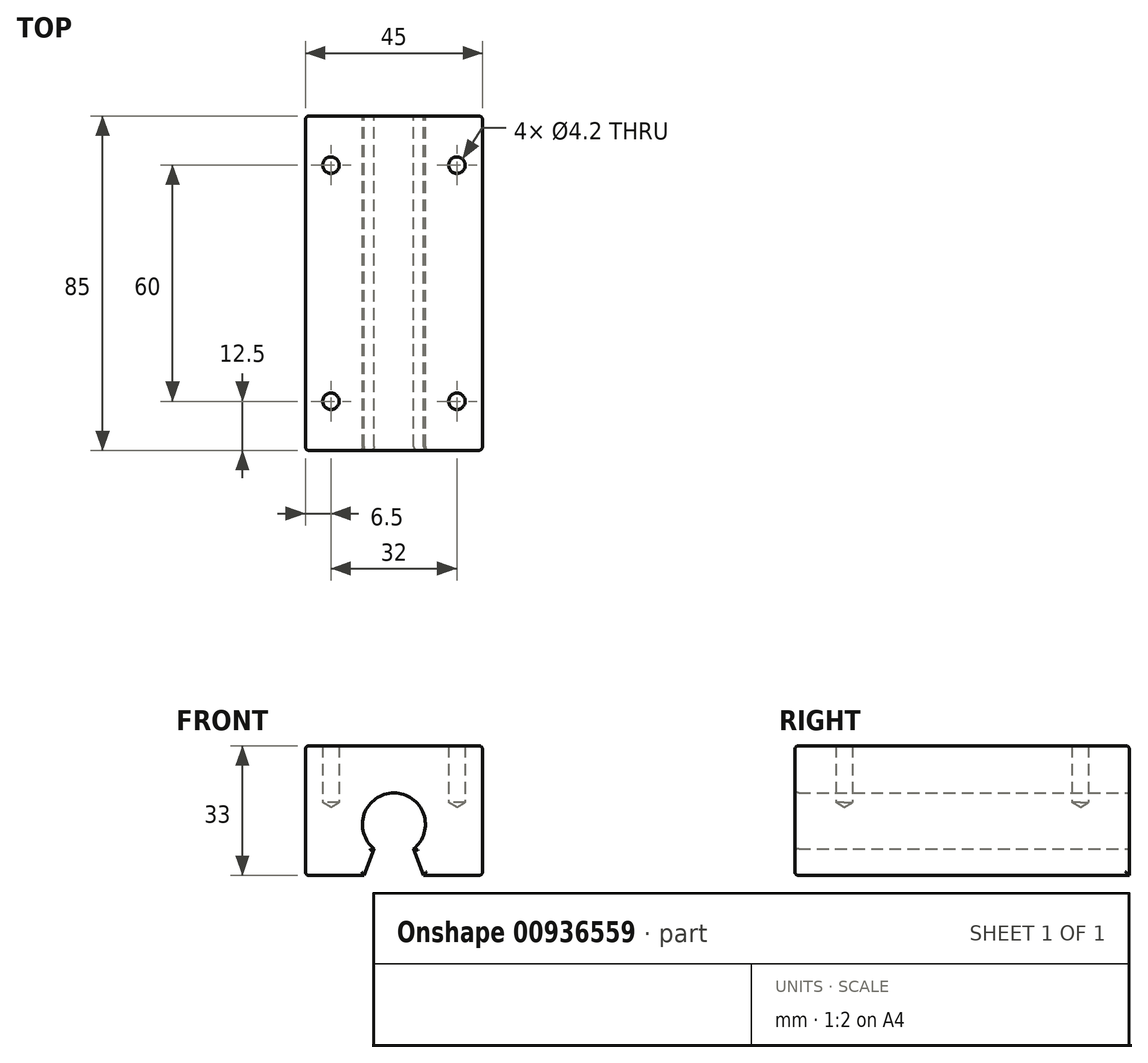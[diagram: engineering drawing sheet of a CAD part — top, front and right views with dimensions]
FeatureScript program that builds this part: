
annotation { "Feature Type Name" : "Feature", "Feature Type Description" : "" }
export const myFeature = defineFeature(function(context is Context, id is Id, definition is map)
    precondition{}
    {
        {
            var Q0;
            Q0=qCreatedBy(makeId("Front.planeOp"),FACE);
            var sketch = newSketch(context, id + "F0", { "sketchPlane" : qUnion([Q0])});
            skLineSegment(sketch, "E0.bottom", {"start": v(-22.5, 16.5) * mm, "end": v(22.5, 16.5) * mm});
            skLineSegment(sketch, "E0.top", {"start": v(-22.5, -16.5) * mm, "end": v(-7.57, -16.5) * mm});
            skLineSegment(sketch, "E0.left", {"start": v(-22.5, 16.5) * mm, "end": v(-22.5, -16.5) * mm});
            skLineSegment(sketch, "E0.right", {"start": v(22.5, 16.5) * mm, "end": v(22.5, -16.5) * mm});
            skPoint(sketch, "E0.middle", {"position": v(0, 0) * mm});
            skArc(sketch, "E1", {"start": v(5, -9.74) * mm, "mid": v(0, 4.5) * mm, "end": v(-5, -9.74) * mm});
            skLineSegment(sketch, "E2", {"start": v(-5, -9.74) * mm, "end": v(-7.57, -16.5) * mm});
            skPoint(sketch, "E3.MirrorP", {"position": v(-2.27, 0.86) * mm});
            skLineSegment(sketch, "E4", {"start": v(0, 23.1) * mm, "end": v(0, -23.77) * mm, "construction": true});
            skLineSegment(sketch, "E5.MirrorCS", {"start": v(5, -9.74) * mm, "end": v(7.57, -16.5) * mm});
            skLineSegment(sketch, "E6.trimOffspring", {"start": v(7.57, -16.5) * mm, "end": v(22.5, -16.5) * mm});
            skSolve(sketch);
        }
        {
            var Q0;
            Q0=makeQuery(id+"F0.imprint","IMPRINT",FACE,{"disambiguationData":[TD([[makeQuery(id+"F0.imprint","IMPRINT",EDGE,{"derivedFrom":sQuery(id+"F0.wireOp",EDGE,"E0.bottom")}),-1.0]])]});
            extrude(context, id + "F1", {"entities" : qUnion([Q0]), "depth" : 85 * mm, "offsetDistance" : 25 * mm});
        }
        {
            var Q0;
            Q0=makeQuery(id+"F1.opExtrude","SWEPT_FACE",FACE,{"disambiguationData":[OSD([sQuery(id+"F0.wireOp",EDGE,"E0.left")])]});
            var Q1;
            Q1=makeQuery(id+"F1.opExtrude","SWEPT_FACE",FACE,{"disambiguationData":[OSD([sQuery(id+"F0.wireOp",EDGE,"E0.bottom")])]});
            var Q2;
            Q2=makeQuery(id+"F1.opExtrude","CAP_FACE",FACE,{"disambiguationData":[OSD([sQuery(id+"F0.wireOp",EDGE,"E0.bottom"),sQuery(id+"F0.wireOp",EDGE,"E0.top"),sQuery(id+"F0.wireOp",EDGE,"E0.left"),sQuery(id+"F0.wireOp",EDGE,"E0.right"),sQuery(id+"F0.wireOp",EDGE,"E1"),sQuery(id+"F0.wireOp",EDGE,"E2"),sQuery(id+"F0.wireOp",EDGE,"E5.MirrorCS"),sQuery(id+"F0.wireOp",EDGE,"E6.trimOffspring")])],"isStart":false});
            var Q3;
            Q3=makeQuery(id+"F1.opExtrude","SWEPT_FACE",FACE,{"disambiguationData":[OSD([sQuery(id+"F0.wireOp",EDGE,"E0.right")])]});
            fillet(context, id + "F2", {"entities" : qUnion([Q0, Q1, Q2, Q3]), "radius" : 1 * mm, "tangentPropagation" : true, "allowEdgeOverflow" : false});
        }
        {
            var Q0;
            Q0=makeQuery(id+"F1.opExtrude","SWEPT_FACE",FACE,{"disambiguationData":[OSD([sQuery(id+"F0.wireOp",EDGE,"E0.bottom")])]});
            var sketch = newSketch(context, id + "F3", { "sketchPlane" : qUnion([Q0])});
            skLineSegment(sketch, "E7", {"start": v(0, 0) * mm, "end": v(0, -84) * mm, "construction": true});
            skPoint(sketch, "E8", {"position": v(-16, -12.5) * mm});
            skPoint(sketch, "E9", {"position": v(-16, -72.5) * mm});
            skPoint(sketch, "E10.MirrorP", {"position": v(16, -12.5) * mm});
            skPoint(sketch, "E11.MirrorP", {"position": v(16, -72.5) * mm});
            skSolve(sketch);
        }
        {
            var Q0;
            Q0=sQuery(id+"F3.wireOp",VERTEX,"E8");
            var Q1;
            Q1=sQuery(id+"F3.wireOp",VERTEX,"E10.MirrorP");
            var Q2;
            Q2=sQuery(id+"F3.wireOp",VERTEX,"E9");
            var Q3;
            Q3=sQuery(id+"F3.wireOp",VERTEX,"E11.MirrorP");
            var Q4;
            Q4=makeQuery(id+"F1.opExtrude","SWEPT_BODY",BODY,{"disambiguationData":[OSD([sQuery(id+"F0.wireOp",EDGE,"E0.bottom"),sQuery(id+"F0.wireOp",EDGE,"E0.top"),sQuery(id+"F0.wireOp",EDGE,"E0.left"),sQuery(id+"F0.wireOp",EDGE,"E0.right"),sQuery(id+"F0.wireOp",EDGE,"E1"),sQuery(id+"F0.wireOp",EDGE,"E2"),sQuery(id+"F0.wireOp",EDGE,"E5.MirrorCS"),sQuery(id+"F0.wireOp",EDGE,"E6.trimOffspring")])]});
            hole(context, id + "F4", {"style" : HoleStyle.SIMPLE, "endStyle" : HoleEndStyle.BLIND, "standardTappedOrClearance" : lookupTablePath({ "standard" : "ISO", "engagement" : "75%", "pitch" : "0.8 mm", "size" : "M5", "type" : "Tapped" }), "standardBlindInLast" : lookupTablePath({ "standard" : "ISO", "engagement" : "75%", "pitch" : "0.8 mm", "size" : "M5", "type" : "Tapped" }), "holeDiameter" : 4.2 * mm, "majorDiameter" : 5 * mm, "showTappedDepth" : true, "holeDepth" : 14.4 * mm, "isTappedThrough" : true, "tappedDepth" : 12 * mm, "tapClearance" : 3, "locations" : qUnion([Q0, Q1, Q2, Q3]), "scope" : qUnion([Q4]), "startStyle" : HoleStartStyle.PART});
        }
    });
